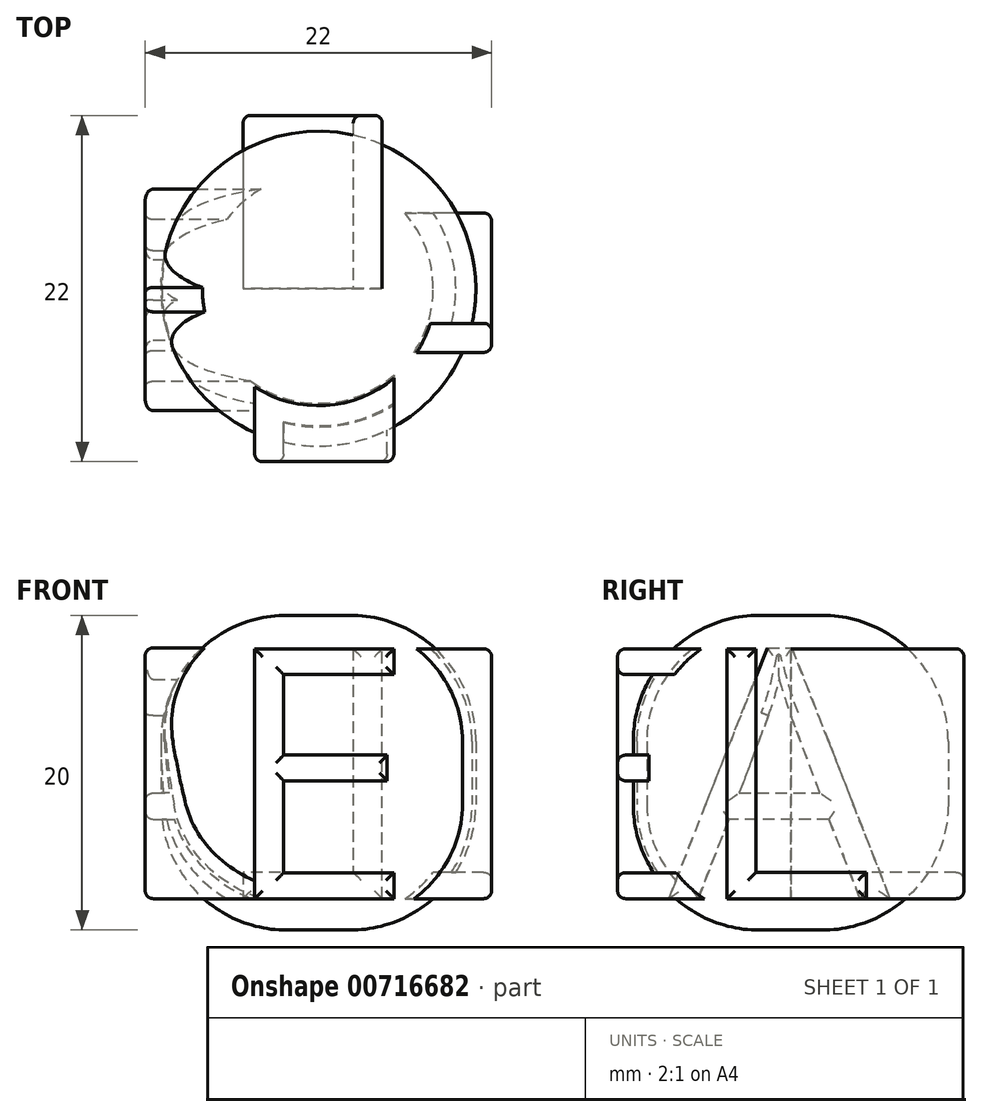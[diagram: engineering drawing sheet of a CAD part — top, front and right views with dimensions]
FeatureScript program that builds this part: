
annotation { "Feature Type Name" : "Feature", "Feature Type Description" : "" }
export const myFeature = defineFeature(function(context is Context, id is Id, definition is map)
    precondition{}
    {
        {
            var Q0;
            Q0=qCreatedBy(makeId("Top.planeOp"),FACE);
            var sketch = newSketch(context, id + "F0", { "sketchPlane" : qUnion([Q0])});
            skLineSegment(sketch, "E0.bottom", {"start": v(0, -10) * mm, "end": v(0, -10) * mm});
            skLineSegment(sketch, "E0.top", {"start": v(0, 10) * mm, "end": v(0, 10) * mm});
            skLineSegment(sketch, "E0.left", {"start": v(10, 0) * mm, "end": v(10, 0) * mm});
            skLineSegment(sketch, "E0.right", {"start": v(-10, 0) * mm, "end": v(-10, 0) * mm});
            skPoint(sketch, "E0.middle", {"position": v(0, 0) * mm});
            skPoint(sketch, "E1.visualSharp", {"position": v(-10, 10) * mm});
            skArc(sketch, "E1.filletArc", {"start": v(0, 10) * mm, "mid": v(-7.07, 7.07) * mm, "end": v(-10, 0) * mm});
            skPoint(sketch, "E2.visualSharp", {"position": v(10, 10) * mm});
            skArc(sketch, "E2.filletArc", {"start": v(10, 0) * mm, "mid": v(7.07, 7.07) * mm, "end": v(0, 10) * mm});
            skPoint(sketch, "E3.visualSharp", {"position": v(10, -10) * mm});
            skArc(sketch, "E3.filletArc", {"start": v(0, -10) * mm, "mid": v(7.07, -7.07) * mm, "end": v(10, 0) * mm});
            skPoint(sketch, "E4.visualSharp", {"position": v(-10, -10) * mm});
            skArc(sketch, "E4.filletArc", {"start": v(-10, 0) * mm, "mid": v(-7.07, -7.07) * mm, "end": v(0, -10) * mm});
            skSolve(sketch);
        }
        {
            var Q0;
            Q0=makeQuery(id+"F0.imprint","IMPRINT",FACE,{"disambiguationData":[TD([[makeQuery(id+"F0.imprint","IMPRINT",EDGE,{"derivedFrom":sQuery(id+"F0.wireOp",EDGE,"E1.filletArc")}),1.0]])]});
            extrude(context, id + "F1", {"entities" : qUnion([Q0]), "depth" : 20 * mm, "offsetDistance" : 25 * mm});
        }
        {
            var Q0;
            Q0=makeQuery(id+"F1.opExtrude","CAP_FACE",FACE,{"disambiguationData":[OSD([sQuery(id+"F0.wireOp",EDGE,"E0.bottom"),sQuery(id+"F0.wireOp",EDGE,"E0.top"),sQuery(id+"F0.wireOp",EDGE,"E0.left"),sQuery(id+"F0.wireOp",EDGE,"E0.right"),sQuery(id+"F0.wireOp",EDGE,"E1.filletArc"),sQuery(id+"F0.wireOp",EDGE,"E2.filletArc"),sQuery(id+"F0.wireOp",EDGE,"E3.filletArc"),sQuery(id+"F0.wireOp",EDGE,"E4.filletArc")])],"isStart":false});
            var Q1;
            Q1=makeQuery(id+"F1.opExtrude","CAP_FACE",FACE,{"disambiguationData":[OSD([sQuery(id+"F0.wireOp",EDGE,"E0.bottom"),sQuery(id+"F0.wireOp",EDGE,"E0.top"),sQuery(id+"F0.wireOp",EDGE,"E0.left"),sQuery(id+"F0.wireOp",EDGE,"E0.right"),sQuery(id+"F0.wireOp",EDGE,"E1.filletArc"),sQuery(id+"F0.wireOp",EDGE,"E2.filletArc"),sQuery(id+"F0.wireOp",EDGE,"E3.filletArc"),sQuery(id+"F0.wireOp",EDGE,"E4.filletArc")])],"isStart":true});
            fillet(context, id + "F2", {"entities" : qUnion([Q0, Q1]), "radius" : 8 * mm, "tangentPropagation" : true, "allowEdgeOverflow" : false});
        }
        {
            var Q0;
            Q0=qCreatedBy(makeId("Front.planeOp"),FACE);
            var sketch = newSketch(context, id + "F3", { "sketchPlane" : qUnion([Q0])});
            skText(sketch, "E5", { "text": "E", "fontName": "OpenSans-Regular.ttf"});
            skLineSegment(sketch, "E6", {"start": v(0, 0) * mm, "end": v(0, 2) * mm, "construction": true});
            const initialGuessF3  = {"E5": [-0.00623, 0.002, 1, 0, 0.016]};
            skSetInitialGuess(sketch, initialGuessF3);
            skSolve(sketch);
        }
        {
            var Q0;
            Q0=qCreatedBy(makeId("Right.planeOp"),FACE);
            var sketch = newSketch(context, id + "F4", { "sketchPlane" : qUnion([Q0])});
            skText(sketch, "E7", { "text": "L", "fontName": "OpenSans-Regular.ttf"});
            skLineSegment(sketch, "E8", {"start": v(0, 0) * mm, "end": v(0, 2) * mm, "construction": true});
            const initialGuessF4  = {"E7": [-0.00623, 0.002, 1, 0, 0.016]};
            skSetInitialGuess(sketch, initialGuessF4);
            skSolve(sketch);
        }
        {
            var Q0;
            Q0=qCreatedBy(makeId("Front.planeOp"),FACE);
            var sketch = newSketch(context, id + "F5", { "sketchPlane" : qUnion([Q0])});
            skText(sketch, "E9", { "text": "L", "fontName": "OpenSans-Regular.ttf"});
            skLineSegment(sketch, "E10", {"start": v(0, 0) * mm, "end": v(0, 2) * mm, "construction": true});
            const initialGuessF5  = {"E9": [-0.00623, 0.002, 1, 0, 0.016]};
            skSetInitialGuess(sketch, initialGuessF5);
            skSolve(sketch);
        }
        {
            var Q0;
            Q0=qCreatedBy(makeId("Right.planeOp"),FACE);
            var sketch = newSketch(context, id + "F6", { "sketchPlane" : qUnion([Q0])});
            skText(sketch, "E11", { "text": "A", "fontName": "OpenSans-Regular.ttf"});
            skLineSegment(sketch, "E12", {"start": v(0, 0) * mm, "end": v(0, 2) * mm, "construction": true});
            const initialGuessF6  = {"E11": [-0.00775, 0.002, 1, 0, 0.016]};
            skSetInitialGuess(sketch, initialGuessF6);
            skSolve(sketch);
        }
        {
            var Q0;
            Q0 = qSketchRegion(id + "F3", true);
            extrude(context, id + "F7", {"entities" : qUnion([Q0]), "operationType" : NewBodyOperationType.ADD, "depth" : 11 * mm, "offsetDistance" : 25 * mm});
        }
        {
            var Q0;
            Q0 = qSketchRegion(id + "F4", true);
            extrude(context, id + "F8", {"entities" : qUnion([Q0]), "operationType" : NewBodyOperationType.ADD, "depth" : 11 * mm, "offsetDistance" : 25 * mm});
        }
        {
            var Q0;
            Q0 = qSketchRegion(id + "F5", true);
            extrude(context, id + "F9", {"entities" : qUnion([Q0]), "operationType" : NewBodyOperationType.ADD, "depth" : 2 * mm, "offsetDistance" : 25 * mm});
        }
        {
            var Q0;
            Q0 = qSketchRegion(id + "F6", true);
            extrude(context, id + "F10", {"entities" : qUnion([Q0]), "operationType" : NewBodyOperationType.ADD, "oppositeDirection" : true, "depth" : 11 * mm, "offsetDistance" : 25 * mm});
        }
        {
            var Q0;
            Q0 = qSketchRegion(id + "F5", true);
            extrude(context, id + "F11", {"entities" : qUnion([Q0]), "depth" : 11 * mm, "offsetDistance" : 25 * mm});
        }
        {
            var Q0;
            Q0=makeQuery(id+"F11.opExtrude","SWEPT_BODY",BODY,{"disambiguationData":[OSD([sQuery(id+"F5.wireOp",EDGE,"E9.sketch_text.stroke-0"),sQuery(id+"F5.wireOp",EDGE,"E9.sketch_text.stroke-1"),sQuery(id+"F5.wireOp",EDGE,"E9.sketch_text.stroke-2"),sQuery(id+"F5.wireOp",EDGE,"E9.sketch_text.stroke-3"),sQuery(id+"F5.wireOp",EDGE,"E9.sketch_text.stroke-4"),sQuery(id+"F5.wireOp",EDGE,"E9.sketch_text.stroke-5")])]});
            var Q1;
            Q1=sQuery(id+"F5.wireOp",EDGE,"E9.sketch_text.center");
            transform(context, id + "F12", {"entities" : qUnion([Q0]), "transformType" : TransformType.ROTATION, "transformAxis" : qUnion([Q1]), "angle" : 180 * degree, "makeCopy" : false});
        }
        {
            var Q0;
            Q0=makeQuery(id+"F7.opExtrude","CAP_FACE",FACE,{"disambiguationData":[OSD([sQuery(id+"F3.wireOp",EDGE,"E5.sketch_text.stroke-0"),sQuery(id+"F3.wireOp",EDGE,"E5.sketch_text.stroke-1"),sQuery(id+"F3.wireOp",EDGE,"E5.sketch_text.stroke-2"),sQuery(id+"F3.wireOp",EDGE,"E5.sketch_text.stroke-3"),sQuery(id+"F3.wireOp",EDGE,"E5.sketch_text.stroke-4"),sQuery(id+"F3.wireOp",EDGE,"E5.sketch_text.stroke-5"),sQuery(id+"F3.wireOp",EDGE,"E5.sketch_text.stroke-6"),sQuery(id+"F3.wireOp",EDGE,"E5.sketch_text.stroke-7"),sQuery(id+"F3.wireOp",EDGE,"E5.sketch_text.stroke-8"),sQuery(id+"F3.wireOp",EDGE,"E5.sketch_text.stroke-9"),sQuery(id+"F3.wireOp",EDGE,"E5.sketch_text.stroke-10"),sQuery(id+"F3.wireOp",EDGE,"E5.sketch_text.stroke-11")])],"isStart":false});
            var Q1;
            Q1=makeQuery(id+"F8.opExtrude","CAP_FACE",FACE,{"disambiguationData":[OSD([sQuery(id+"F4.wireOp",EDGE,"E7.sketch_text.stroke-0"),sQuery(id+"F4.wireOp",EDGE,"E7.sketch_text.stroke-1"),sQuery(id+"F4.wireOp",EDGE,"E7.sketch_text.stroke-2"),sQuery(id+"F4.wireOp",EDGE,"E7.sketch_text.stroke-3"),sQuery(id+"F4.wireOp",EDGE,"E7.sketch_text.stroke-4"),sQuery(id+"F4.wireOp",EDGE,"E7.sketch_text.stroke-5")])],"isStart":false});
            var Q2;
            Q2=makeQuery(id+"F10.opExtrude","CAP_FACE",FACE,{"disambiguationData":[OSD([sQuery(id+"F6.wireOp",EDGE,"E11.sketch_text.stroke-0"),sQuery(id+"F6.wireOp",EDGE,"E11.sketch_text.stroke-1"),sQuery(id+"F6.wireOp",EDGE,"E11.sketch_text.stroke-2"),sQuery(id+"F6.wireOp",EDGE,"E11.sketch_text.stroke-3"),sQuery(id+"F6.wireOp",EDGE,"E11.sketch_text.stroke-4"),sQuery(id+"F6.wireOp",EDGE,"E11.sketch_text.stroke-5"),sQuery(id+"F6.wireOp",EDGE,"E11.sketch_text.stroke-6"),sQuery(id+"F6.wireOp",EDGE,"E11.sketch_text.stroke-7"),sQuery(id+"F6.wireOp",EDGE,"E11.sketch_text.stroke-8"),sQuery(id+"F6.wireOp",EDGE,"E11.sketch_text.stroke-9"),sQuery(id+"F6.wireOp",EDGE,"E11.sketch_text.stroke-10"),sQuery(id+"F6.wireOp",EDGE,"E11.sketch_text.stroke-11"),sQuery(id+"F6.wireOp",EDGE,"E11.sketch_text.stroke-12")])],"isStart":false});
            var Q3;
            Q3=makeQuery(id+"F11.opExtrude","CAP_FACE",FACE,{"disambiguationData":[OSD([sQuery(id+"F5.wireOp",EDGE,"E9.sketch_text.stroke-0"),sQuery(id+"F5.wireOp",EDGE,"E9.sketch_text.stroke-1"),sQuery(id+"F5.wireOp",EDGE,"E9.sketch_text.stroke-2"),sQuery(id+"F5.wireOp",EDGE,"E9.sketch_text.stroke-3"),sQuery(id+"F5.wireOp",EDGE,"E9.sketch_text.stroke-4"),sQuery(id+"F5.wireOp",EDGE,"E9.sketch_text.stroke-5")])],"isStart":false});
            fillet(context, id + "F13", {"entities" : qUnion([Q0, Q1, Q2, Q3]), "radius" : .5 * mm, "allowEdgeOverflow" : false});
        }
    });
